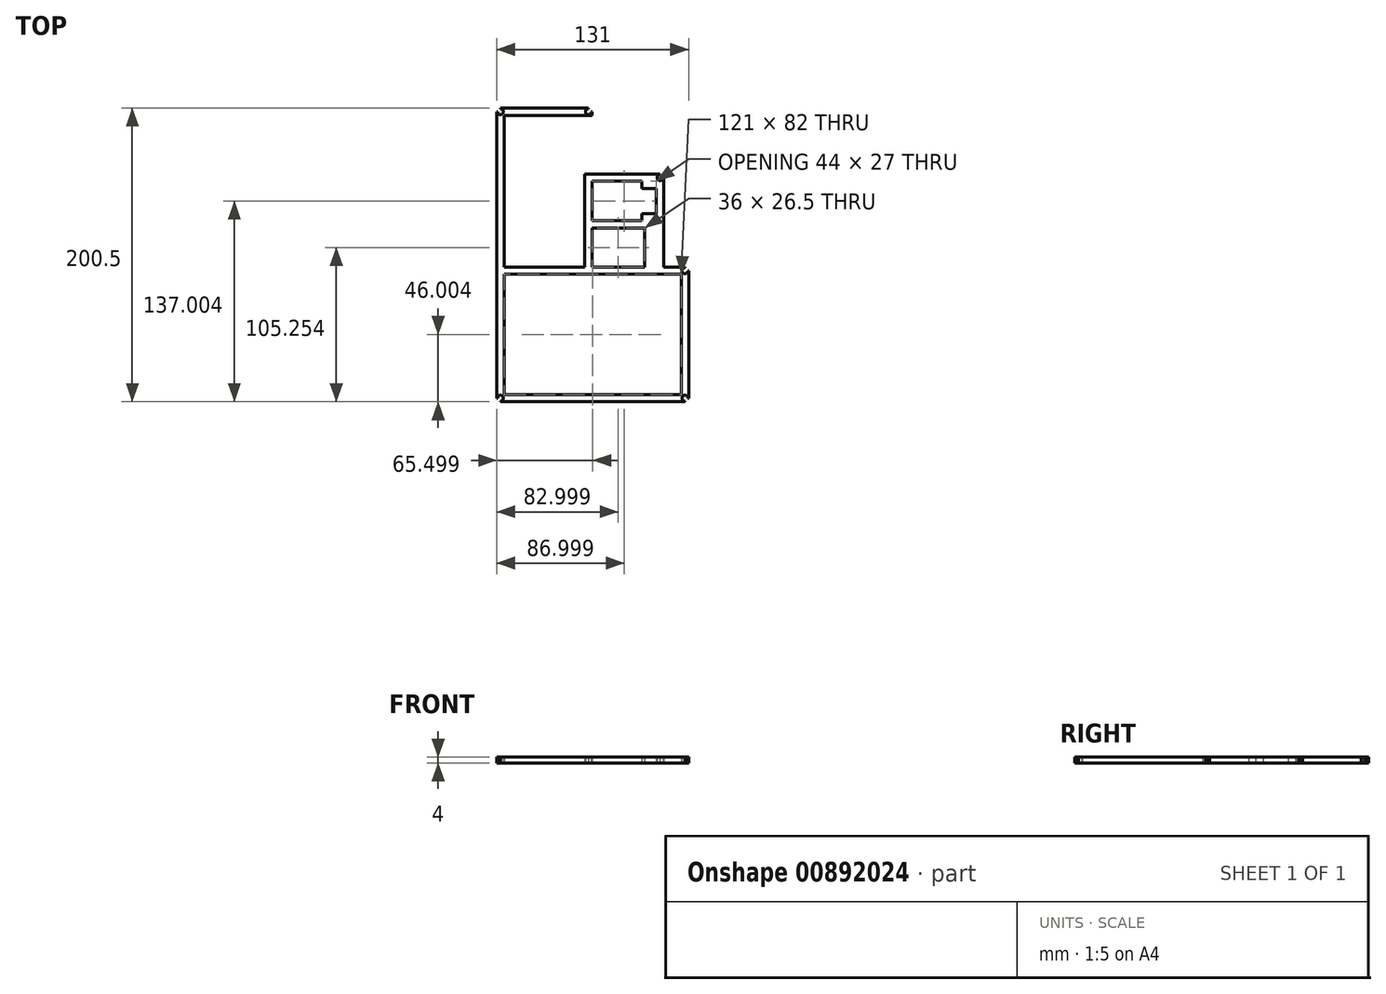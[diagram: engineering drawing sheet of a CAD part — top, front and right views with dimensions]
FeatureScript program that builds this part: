
annotation { "Feature Type Name" : "Feature", "Feature Type Description" : "" }
export const myFeature = defineFeature(function(context is Context, id is Id, definition is map)
    precondition{}
    {
        {
            var Q0;
            Q0=qCreatedBy(makeId("Top.planeOp"),FACE);
            var sketch = newSketch(context, id + "F0", { "sketchPlane" : qUnion([Q0])});
            skLineSegment(sketch, "E0.bottom", {"start": v(-40.7, -58.83) * mm, "end": v(14.3, -58.83) * mm});
            skLineSegment(sketch, "E0.top", {"start": v(-40.7, 44.67) * mm, "end": v(14.3, 44.67) * mm});
            skLineSegment(sketch, "E0.left", {"start": v(-40.7, -58.83) * mm, "end": v(-40.7, 44.67) * mm});
            skLineSegment(sketch, "E0.right", {"start": v(14.3, -58.83) * mm, "end": v(14.3, 44.67) * mm});
            skLineSegment(sketch, "E1.bottom", {"start": v(-45.7, 49.67) * mm, "end": v(85.3, 49.67) * mm});
            skLineSegment(sketch, "E1.top", {"start": v(-45.7, -150.83) * mm, "end": v(85.3, -150.83) * mm});
            skLineSegment(sketch, "E1.left", {"start": v(-45.7, 49.67) * mm, "end": v(-45.7, -150.83) * mm});
            skLineSegment(sketch, "E1.right", {"start": v(85.3, 49.67) * mm, "end": v(85.3, -150.83) * mm});
            skLineSegment(sketch, "E2.bottom", {"start": v(-40.7, -63.83) * mm, "end": v(80.3, -63.83) * mm});
            skLineSegment(sketch, "E2.top", {"start": v(-40.7, -145.83) * mm, "end": v(80.3, -145.83) * mm});
            skLineSegment(sketch, "E2.left", {"start": v(-40.7, -63.83) * mm, "end": v(-40.7, -145.83) * mm});
            skLineSegment(sketch, "E2.right", {"start": v(80.3, -63.83) * mm, "end": v(80.3, -145.83) * mm});
            skLineSegment(sketch, "E3.top", {"start": v(14.3, -63.83) * mm, "end": v(19.3, -63.83) * mm});
            skLineSegment(sketch, "E4.bottom", {"start": v(19.3, -58.83) * mm, "end": v(55.3, -58.83) * mm});
            skLineSegment(sketch, "E4.top", {"start": v(19.3, -32.33) * mm, "end": v(55.3, -32.33) * mm});
            skLineSegment(sketch, "E4.left", {"start": v(19.3, -58.83) * mm, "end": v(19.3, -32.33) * mm});
            skLineSegment(sketch, "E4.right", {"start": v(55.3, -58.83) * mm, "end": v(55.3, -32.33) * mm});
            skLineSegment(sketch, "E5.right", {"start": v(14.3, -32.33) * mm, "end": v(14.3, -27.33) * mm});
            skLineSegment(sketch, "E6.bottom", {"start": v(19.3, -27.33) * mm, "end": v(53.3, -27.33) * mm});
            skLineSegment(sketch, "E6.top", {"start": v(19.3, -0.33) * mm, "end": v(53.3, -0.33) * mm});
            skLineSegment(sketch, "E6.left", {"start": v(19.3, -27.33) * mm, "end": v(19.3, -0.33) * mm});
            skLineSegment(sketch, "E6.right", {"start": v(53.3, -27.33) * mm, "end": v(53.3, -0.33) * mm});
            skLineSegment(sketch, "E7", {"start": v(53.3, -27.33) * mm, "end": v(53.3, -22.33) * mm});
            skLineSegment(sketch, "E8", {"start": v(53.3, -22.33) * mm, "end": v(53.3, -5.33) * mm});
            skLineSegment(sketch, "E9.bottom", {"start": v(53.3, -5.33) * mm, "end": v(53.3, -5.33) * mm});
            skLineSegment(sketch, "E9.top", {"start": v(53.3, -22.33) * mm, "end": v(53.3, -22.33) * mm});
            skLineSegment(sketch, "E9.left", {"start": v(53.3, -5.33) * mm, "end": v(53.3, -22.33) * mm});
            skLineSegment(sketch, "E9.right", {"start": v(53.3, -5.33) * mm, "end": v(53.3, -22.33) * mm});
            skLineSegment(sketch, "E10.bottom", {"start": v(53.3, -22.33) * mm, "end": v(63.3, -22.33) * mm});
            skLineSegment(sketch, "E10.top", {"start": v(53.3, -5.33) * mm, "end": v(63.3, -5.33) * mm});
            skLineSegment(sketch, "E10.right", {"start": v(63.3, -22.33) * mm, "end": v(63.3, -5.33) * mm});
            skLineSegment(sketch, "E11.bottom", {"start": v(14.3, 44.67) * mm, "end": v(19.3, 44.67) * mm});
            skLineSegment(sketch, "E11.top", {"start": v(14.3, 49.67) * mm, "end": v(19.3, 49.67) * mm});
            skLineSegment(sketch, "E11.left", {"start": v(14.3, 44.67) * mm, "end": v(14.3, 49.67) * mm});
            skLineSegment(sketch, "E11.right", {"start": v(19.3, 44.67) * mm, "end": v(19.3, 49.67) * mm});
            skLineSegment(sketch, "E12.bottom", {"start": v(19.3, -0.33) * mm, "end": v(14.3, -0.33) * mm});
            skLineSegment(sketch, "E12.top", {"start": v(19.3, 4.67) * mm, "end": v(14.3, 4.67) * mm});
            skLineSegment(sketch, "E12.left", {"start": v(19.3, -0.33) * mm, "end": v(19.3, 4.67) * mm});
            skLineSegment(sketch, "E12.right", {"start": v(14.3, -0.33) * mm, "end": v(14.3, 4.67) * mm});
            skLineSegment(sketch, "E13.bottom", {"start": v(85.3, 49.67) * mm, "end": v(80.3, 49.67) * mm});
            skLineSegment(sketch, "E13.left", {"start": v(85.3, 49.67) * mm, "end": v(85.3, 44.67) * mm});
            skLineSegment(sketch, "E14.top", {"start": v(19.3, 49.67) * mm, "end": v(85.3, 49.67) * mm});
            skLineSegment(sketch, "E14.left", {"start": v(19.3, 4.67) * mm, "end": v(19.3, 49.67) * mm});
            skLineSegment(sketch, "E14.right", {"start": v(85.3, 4.67) * mm, "end": v(85.3, 49.67) * mm});
            skLineSegment(sketch, "E15.bottom", {"start": v(80.3, -63.83) * mm, "end": v(85.3, -63.83) * mm});
            skLineSegment(sketch, "E15.top", {"start": v(80.3, -58.83) * mm, "end": v(85.3, -58.83) * mm});
            skLineSegment(sketch, "E15.left", {"start": v(80.3, -63.83) * mm, "end": v(80.3, -58.83) * mm});
            skLineSegment(sketch, "E15.right", {"start": v(85.3, -63.83) * mm, "end": v(85.3, -58.83) * mm});
            skLineSegment(sketch, "E16", {"start": v(63.3, -5.33) * mm, "end": v(68.3, -5.33) * mm});
            skLineSegment(sketch, "E17", {"start": v(68.3, -5.33) * mm, "end": v(68.3, -22.33) * mm});
            skLineSegment(sketch, "E18.bottom", {"start": v(85.3, -58.83) * mm, "end": v(68.3, -58.83) * mm});
            skLineSegment(sketch, "E18.left", {"start": v(85.3, -58.83) * mm, "end": v(85.3, 4.67) * mm});
            skLineSegment(sketch, "E18.right", {"start": v(68.3, -58.83) * mm, "end": v(68.3, 4.67) * mm});
            skLineSegment(sketch, "E19", {"start": v(19.3, 4.67) * mm, "end": v(68.3, 4.67) * mm});
            skLineSegment(sketch, "E20.bottom", {"start": v(68.3, 4.67) * mm, "end": v(65.8, 4.67) * mm});
            skLineSegment(sketch, "E20.top", {"start": v(68.3, 2.17) * mm, "end": v(65.8, 2.17) * mm});
            skLineSegment(sketch, "E20.left", {"start": v(68.3, 4.67) * mm, "end": v(68.3, 2.17) * mm});
            skLineSegment(sketch, "E20.right", {"start": v(65.8, 4.67) * mm, "end": v(65.8, 2.17) * mm});
            skLineSegment(sketch, "E21.bottom", {"start": v(19.3, 44.67) * mm, "end": v(16.8, 44.67) * mm});
            skLineSegment(sketch, "E21.top", {"start": v(19.3, 47.17) * mm, "end": v(16.8, 47.17) * mm});
            skLineSegment(sketch, "E21.left", {"start": v(19.3, 44.67) * mm, "end": v(19.3, 47.17) * mm});
            skLineSegment(sketch, "E22.bottom", {"start": v(85.3, -58.83) * mm, "end": v(82.8, -58.83) * mm});
            skLineSegment(sketch, "E22.top", {"start": v(85.3, -61.33) * mm, "end": v(82.8, -61.33) * mm});
            skLineSegment(sketch, "E22.left", {"start": v(85.3, -58.83) * mm, "end": v(85.3, -61.33) * mm});
            skLineSegment(sketch, "E22.right", {"start": v(82.8, -58.83) * mm, "end": v(82.8, -61.33) * mm});
            skLineSegment(sketch, "E23.bottom", {"start": v(85.3, -150.83) * mm, "end": v(82.8, -150.83) * mm});
            skLineSegment(sketch, "E23.top", {"start": v(85.3, -148.33) * mm, "end": v(82.8, -148.33) * mm});
            skLineSegment(sketch, "E23.left", {"start": v(85.3, -150.83) * mm, "end": v(85.3, -148.33) * mm});
            skLineSegment(sketch, "E23.right", {"start": v(82.8, -150.83) * mm, "end": v(82.8, -148.33) * mm});
            skLineSegment(sketch, "E24.bottom", {"start": v(-45.7, -150.83) * mm, "end": v(-43.2, -150.83) * mm});
            skLineSegment(sketch, "E24.top", {"start": v(-45.7, -148.33) * mm, "end": v(-43.2, -148.33) * mm});
            skLineSegment(sketch, "E24.left", {"start": v(-45.7, -150.83) * mm, "end": v(-45.7, -148.33) * mm});
            skLineSegment(sketch, "E24.right", {"start": v(-43.2, -150.83) * mm, "end": v(-43.2, -148.33) * mm});
            skLineSegment(sketch, "E25.bottom", {"start": v(-45.7, 49.67) * mm, "end": v(-43.2, 49.67) * mm});
            skLineSegment(sketch, "E25.top", {"start": v(-45.7, 47.17) * mm, "end": v(-43.2, 47.17) * mm});
            skLineSegment(sketch, "E25.left", {"start": v(-45.7, 49.67) * mm, "end": v(-45.7, 47.17) * mm});
            skLineSegment(sketch, "E25.right", {"start": v(-43.2, 49.67) * mm, "end": v(-43.2, 47.17) * mm});
            skLineSegment(sketch, "E26.bottom", {"start": v(19.3, 49.67) * mm, "end": v(16.8, 49.67) * mm});
            skLineSegment(sketch, "E26.left", {"start": v(19.3, 49.67) * mm, "end": v(19.3, 47.17) * mm});
            skLineSegment(sketch, "E26.right", {"start": v(16.8, 49.67) * mm, "end": v(16.8, 47.17) * mm});
            skCircle(sketch, "E27", {"center": v(16.8, 47.17) * mm, "radius": 2 * mm});
            skCircle(sketch, "E28", {"center": v(65.8, 2.17) * mm, "radius": 2 * mm});
            skCircle(sketch, "E29", {"center": v(82.8, -61.33) * mm, "radius": 2 * mm});
            skCircle(sketch, "E30", {"center": v(82.8, -148.33) * mm, "radius": 2 * mm});
            skCircle(sketch, "E31", {"center": v(-43.2, -148.33) * mm, "radius": 2 * mm});
            skCircle(sketch, "E32", {"center": v(-43.2, 47.17) * mm, "radius": 2 * mm});
            skLineSegment(sketch, "E33.bottom", {"start": v(-40.7, -63.83) * mm, "end": v(-37.3, -63.83) * mm});
            skLineSegment(sketch, "E33.top", {"start": v(-40.7, -67.23) * mm, "end": v(-37.3, -67.23) * mm});
            skLineSegment(sketch, "E33.left", {"start": v(-40.7, -63.83) * mm, "end": v(-40.7, -67.23) * mm});
            skLineSegment(sketch, "E33.right", {"start": v(-37.3, -63.83) * mm, "end": v(-37.3, -67.23) * mm});
            skLineSegment(sketch, "E34.bottom", {"start": v(-40.7, -145.83) * mm, "end": v(-37.3, -145.83) * mm});
            skLineSegment(sketch, "E34.top", {"start": v(-40.7, -142.43) * mm, "end": v(-37.3, -142.43) * mm});
            skLineSegment(sketch, "E34.left", {"start": v(-40.7, -145.83) * mm, "end": v(-40.7, -142.43) * mm});
            skLineSegment(sketch, "E34.right", {"start": v(-37.3, -145.83) * mm, "end": v(-37.3, -142.43) * mm});
            skLineSegment(sketch, "E35.bottom", {"start": v(80.3, -145.83) * mm, "end": v(76.9, -145.83) * mm});
            skLineSegment(sketch, "E35.top", {"start": v(80.3, -142.43) * mm, "end": v(76.9, -142.43) * mm});
            skLineSegment(sketch, "E35.left", {"start": v(80.3, -145.83) * mm, "end": v(80.3, -142.43) * mm});
            skLineSegment(sketch, "E35.right", {"start": v(76.9, -145.83) * mm, "end": v(76.9, -142.43) * mm});
            skLineSegment(sketch, "E36.bottom", {"start": v(80.3, -63.83) * mm, "end": v(76.9, -63.83) * mm});
            skLineSegment(sketch, "E36.top", {"start": v(80.3, -67.23) * mm, "end": v(76.9, -67.23) * mm});
            skLineSegment(sketch, "E36.left", {"start": v(80.3, -63.83) * mm, "end": v(80.3, -67.23) * mm});
            skLineSegment(sketch, "E36.right", {"start": v(76.9, -63.83) * mm, "end": v(76.9, -67.23) * mm});
            skLineSegment(sketch, "E37.bottom", {"start": v(-40.7, -58.83) * mm, "end": v(-37.7, -58.83) * mm});
            skLineSegment(sketch, "E37.top", {"start": v(-40.7, 28.47) * mm, "end": v(-37.7, 28.47) * mm});
            skLineSegment(sketch, "E37.left", {"start": v(-40.7, -58.83) * mm, "end": v(-40.7, 28.47) * mm});
            skLineSegment(sketch, "E37.right", {"start": v(-37.7, -58.83) * mm, "end": v(-37.7, 28.47) * mm});
            skLineSegment(sketch, "E38.bottom", {"start": v(-37.7, -58.83) * mm, "end": v(-40.7, -58.83) * mm});
            skLineSegment(sketch, "E38.top", {"start": v(-37.7, -52.83) * mm, "end": v(-40.7, -52.83) * mm});
            skLineSegment(sketch, "E38.left", {"start": v(-37.7, -58.83) * mm, "end": v(-37.7, -52.83) * mm});
            skLineSegment(sketch, "E38.right", {"start": v(-40.7, -58.83) * mm, "end": v(-40.7, -52.83) * mm});
            skLineSegment(sketch, "E39.bottom", {"start": v(14.3, -58.83) * mm, "end": v(11.3, -58.83) * mm});
            skLineSegment(sketch, "E39.top", {"start": v(14.3, 29.87) * mm, "end": v(11.3, 29.87) * mm});
            skLineSegment(sketch, "E39.left", {"start": v(14.3, -58.83) * mm, "end": v(14.3, 29.87) * mm});
            skLineSegment(sketch, "E39.right", {"start": v(11.3, -58.83) * mm, "end": v(11.3, 29.87) * mm});
            skLineSegment(sketch, "E40.top", {"start": v(14.3, -47.23) * mm, "end": v(11.3, -47.23) * mm});
            skLineSegment(sketch, "E40.left", {"start": v(14.3, -58.83) * mm, "end": v(14.3, -47.23) * mm});
            skLineSegment(sketch, "E40.right", {"start": v(11.3, -58.83) * mm, "end": v(11.3, -47.23) * mm});
            skCircle(sketch, "E41", {"center": v(-37.7, -52.83) * mm, "radius": 2 * mm});
            skCircle(sketch, "E42", {"center": v(-37.7, 28.47) * mm, "radius": 2 * mm});
            skCircle(sketch, "E43", {"center": v(11.3, 29.87) * mm, "radius": 2 * mm});
            skCircle(sketch, "E44", {"center": v(11.3, -47.23) * mm, "radius": 2 * mm});
            skLineSegment(sketch, "E45.bottom", {"start": v(19.3, -0.33) * mm, "end": v(28.55, -0.33) * mm});
            skLineSegment(sketch, "E45.top", {"start": v(19.3, -2.28) * mm, "end": v(28.55, -2.28) * mm});
            skLineSegment(sketch, "E45.left", {"start": v(19.3, -0.33) * mm, "end": v(19.3, -2.28) * mm});
            skLineSegment(sketch, "E45.right", {"start": v(28.55, -0.33) * mm, "end": v(28.55, -2.28) * mm});
            skLineSegment(sketch, "E46.bottom", {"start": v(19.3, -27.33) * mm, "end": v(28.55, -27.33) * mm});
            skLineSegment(sketch, "E46.top", {"start": v(19.3, -25.38) * mm, "end": v(28.55, -25.38) * mm});
            skLineSegment(sketch, "E46.left", {"start": v(19.3, -27.33) * mm, "end": v(19.3, -25.38) * mm});
            skLineSegment(sketch, "E46.right", {"start": v(28.55, -27.33) * mm, "end": v(28.55, -25.38) * mm});
            skLineSegment(sketch, "E47.bottom", {"start": v(53.3, -0.33) * mm, "end": v(51.35, -0.33) * mm});
            skLineSegment(sketch, "E47.top", {"start": v(53.3, -2.28) * mm, "end": v(51.35, -2.28) * mm});
            skLineSegment(sketch, "E47.left", {"start": v(53.3, -0.33) * mm, "end": v(53.3, -2.28) * mm});
            skLineSegment(sketch, "E47.right", {"start": v(51.35, -0.33) * mm, "end": v(51.35, -2.28) * mm});
            skLineSegment(sketch, "E48.bottom", {"start": v(53.3, -27.33) * mm, "end": v(51.35, -27.33) * mm});
            skLineSegment(sketch, "E48.top", {"start": v(53.3, -25.38) * mm, "end": v(51.35, -25.38) * mm});
            skLineSegment(sketch, "E48.left", {"start": v(53.3, -27.33) * mm, "end": v(53.3, -25.38) * mm});
            skLineSegment(sketch, "E48.right", {"start": v(51.35, -27.33) * mm, "end": v(51.35, -25.38) * mm});
            skLineSegment(sketch, "E49.bottom", {"start": v(55.3, -32.33) * mm, "end": v(53.6, -32.33) * mm});
            skLineSegment(sketch, "E49.top", {"start": v(55.3, -34.03) * mm, "end": v(53.6, -34.03) * mm});
            skLineSegment(sketch, "E49.left", {"start": v(55.3, -32.33) * mm, "end": v(55.3, -34.03) * mm});
            skLineSegment(sketch, "E49.right", {"start": v(53.6, -32.33) * mm, "end": v(53.6, -34.03) * mm});
            skLineSegment(sketch, "E50.bottom", {"start": v(55.3, -58.83) * mm, "end": v(53.6, -58.83) * mm});
            skLineSegment(sketch, "E50.top", {"start": v(55.3, -57.13) * mm, "end": v(53.6, -57.13) * mm});
            skLineSegment(sketch, "E50.left", {"start": v(55.3, -58.83) * mm, "end": v(55.3, -57.13) * mm});
            skLineSegment(sketch, "E50.right", {"start": v(53.6, -58.83) * mm, "end": v(53.6, -57.13) * mm});
            skCircle(sketch, "E51", {"center": v(53.6, -34.03) * mm, "radius": 1.2 * mm});
            skCircle(sketch, "E52", {"center": v(53.6, -57.13) * mm, "radius": 1.2 * mm});
            skCircle(sketch, "E53", {"center": v(51.35, -25.38) * mm, "radius": 1.15 * mm});
            skCircle(sketch, "E54", {"center": v(28.55, -25.38) * mm, "radius": 1.15 * mm});
            skCircle(sketch, "E55", {"center": v(28.55, -2.28) * mm, "radius": 1.15 * mm});
            skCircle(sketch, "E56", {"center": v(51.35, -2.28) * mm, "radius": 1.15 * mm});
            skCircle(sketch, "E57", {"center": v(-37.3, -67.23) * mm, "radius": 1.4 * mm});
            skCircle(sketch, "E58", {"center": v(76.9, -67.23) * mm, "radius": 1.4 * mm});
            skCircle(sketch, "E59", {"center": v(-37.3, -142.43) * mm, "radius": 1.4 * mm});
            skCircle(sketch, "E60", {"center": v(76.9, -142.43) * mm, "radius": 1.4 * mm});
            skSolve(sketch);
        }
        {
            var Q0;
            {var subQ1=sQuery(id+"F0.wireOp",EDGE,"E23.bottom");Q0=makeQuery(id+"F0.imprint","IMPRINT",FACE,{"disambiguationData":[TD([[makeQuery(id+"F0.imprint","IMPRINT",EDGE,{"derivedFrom":subQ1}),-1.0]])]});}
            var Q1;
            {var subQ1=sQuery(id+"F0.wireOp",EDGE,"E24.bottom");Q1=makeQuery(id+"F0.imprint","IMPRINT",FACE,{"disambiguationData":[TD([[makeQuery(id+"F0.imprint","IMPRINT",EDGE,{"derivedFrom":subQ1}),1.0]])]});}
            var Q2;
            {var subQ1=sQuery(id+"F0.wireOp",EDGE,"E25.bottom");Q2=makeQuery(id+"F0.imprint","IMPRINT",FACE,{"disambiguationData":[TD([[makeQuery(id+"F0.imprint","IMPRINT",EDGE,{"derivedFrom":subQ1}),-1.0]])]});}
            var Q3;
            {var subQ1=sQuery(id+"F0.wireOp",EDGE,"E22.bottom");Q3=makeQuery(id+"F0.imprint","IMPRINT",FACE,{"disambiguationData":[TD([[makeQuery(id+"F0.imprint","IMPRINT",EDGE,{"derivedFrom":subQ1}),1.0]])]});}
            var Q4;
            {var subQ1=sQuery(id+"F0.wireOp",EDGE,"E26.bottom");Q4=makeQuery(id+"F0.imprint","IMPRINT",FACE,{"disambiguationData":[TD([[makeQuery(id+"F0.imprint","IMPRINT",EDGE,{"derivedFrom":subQ1}),1.0]])]});}
            var Q5;
            Q5=makeQuery(id+"F0.imprint","IMPRINT",FACE,{"disambiguationData":[TD([[makeQuery(id+"F0.imprint","IMPRINT",EDGE,{"derivedFrom":sQuery(id+"F0.wireOp",EDGE,"E15.bottom")}),1.0]])]});
            var Q6;
            Q6=makeQuery(id+"F0.imprint","IMPRINT",FACE,{"disambiguationData":[TD([[makeQuery(id+"F0.imprint","IMPRINT",EDGE,{"derivedFrom":sQuery(id+"F0.wireOp",EDGE,"E11.bottom")}),1.0]])]});
            var Q7;
            Q7=makeQuery(id+"F0.imprint","IMPRINT",FACE,{"disambiguationData":[TD([[makeQuery(id+"F0.imprint","IMPRINT",EDGE,{"derivedFrom":sQuery(id+"F0.wireOp",EDGE,"E0.bottom")}),-1.0]])]});
            var Q8;
            {var subQ0=sQuery(id+"F0.wireOp",EDGE,"E12.bottom");Q8=makeQuery(id+"F0.imprint","IMPRINT",FACE,{"disambiguationData":[TD([[makeQuery(id+"F0.imprint","IMPRINT",EDGE,{"derivedFrom":subQ0}),-1.0]])]});}
            var Q9;
            {var subQ1=sQuery(id+"F0.wireOp",EDGE,"E0.right");Q9=makeQuery(id+"F0.imprint","IMPRINT",FACE,{"disambiguationData":[TD([[makeQuery(id+"F0.imprint","IMPRINT",EDGE,{"derivedFrom":subQ1}),-1.0]])]});}
            var Q10;
            Q10=makeQuery(id+"F0.imprint","IMPRINT",FACE,{"disambiguationData":[TD([[makeQuery(id+"F0.imprint","IMPRINT",EDGE,{"derivedFrom":sQuery(id+"F0.wireOp",EDGE,"E6.top")}),1.0]])]});
            var Q11;
            {var subQ1=sQuery(id+"F0.wireOp",EDGE,"E20.bottom");Q11=makeQuery(id+"F0.imprint","IMPRINT",FACE,{"disambiguationData":[TD([[makeQuery(id+"F0.imprint","IMPRINT",EDGE,{"derivedFrom":subQ1}),1.0]])]});}
            extrude(context, id + "F1", {"entities" : qUnion([Q0, Q1, Q2, Q3, Q4, Q5, Q6, Q7, Q8, Q9, Q10, Q11]), "depth" : 4 * mm, "offsetDistance" : 25 * mm});
        }
    });
